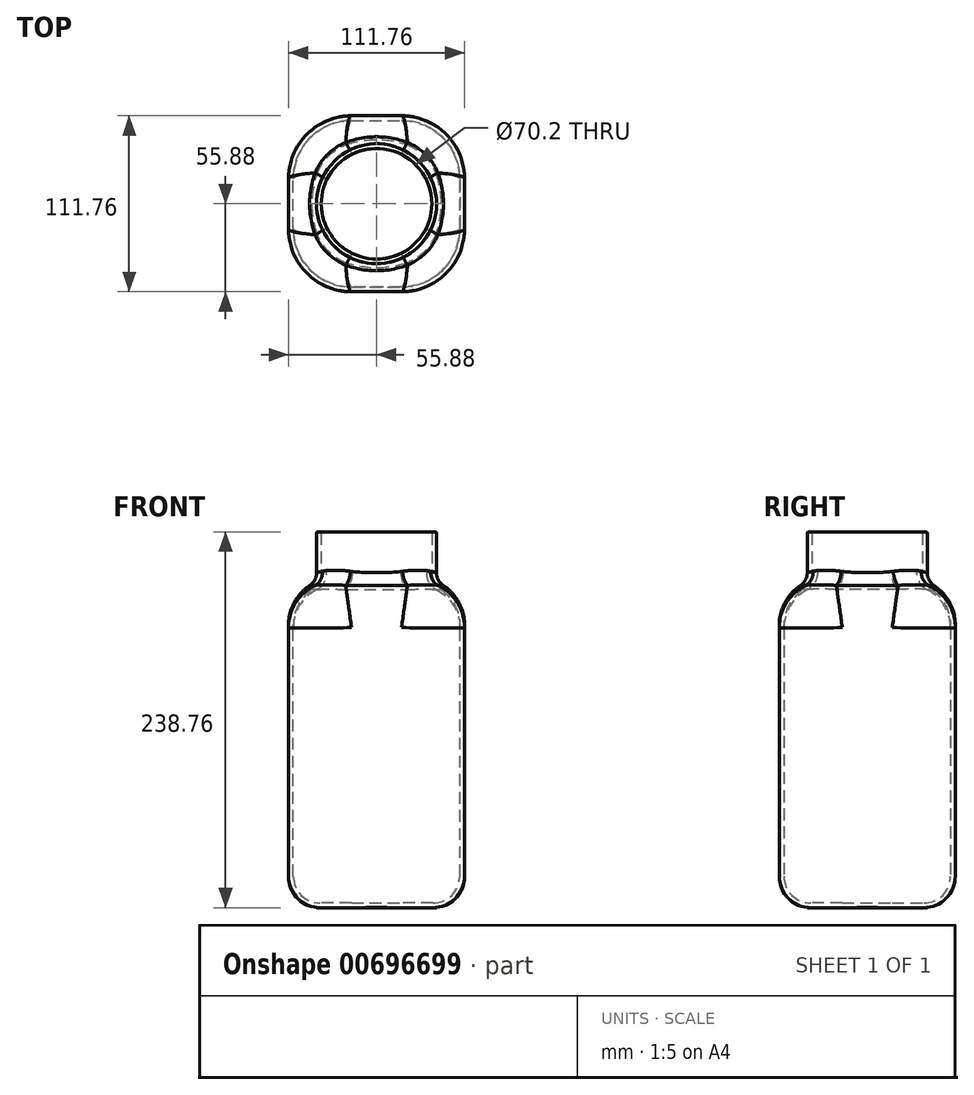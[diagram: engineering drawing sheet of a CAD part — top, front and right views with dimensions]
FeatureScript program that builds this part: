
annotation { "Feature Type Name" : "Feature", "Feature Type Description" : "" }
export const myFeature = defineFeature(function(context is Context, id is Id, definition is map)
    precondition{}
    {
        {
            assignVariable(context, id + "F0", {"name" : "height", "anyValue" : 238.76 * mm});
        }
        {
            var Q0;
            Q0=qCreatedBy(makeId("Top.planeOp"),FACE);
            var sketch = newSketch(context, id + "F1", { "sketchPlane" : qUnion([Q0])});
            skLineSegment(sketch, "E0.bottom", {"start": v(55.88, -55.88) * mm, "end": v(-55.88, -55.88) * mm});
            skLineSegment(sketch, "E0.top", {"start": v(55.88, 55.88) * mm, "end": v(-55.88, 55.88) * mm});
            skLineSegment(sketch, "E0.left", {"start": v(55.88, -55.88) * mm, "end": v(55.88, 55.88) * mm});
            skLineSegment(sketch, "E0.right", {"start": v(-55.88, -55.88) * mm, "end": v(-55.88, 55.88) * mm});
            skPoint(sketch, "E0.middle", {"position": v(0, 0) * mm});
            skCircle(sketch, "E1", {"center": v(0, 0) * mm, "radius": 38.1 * mm});
            skSolve(sketch);
        }
        {
            var Q0;
            Q0=makeQuery(id+"F1.imprint","IMPRINT",FACE,{"disambiguationData":[TD([[makeQuery(id+"F1.imprint","IMPRINT",EDGE,{"derivedFrom":sQuery(id+"F1.wireOp",EDGE,"E0.bottom")}),-1.0]])]});
            extrude(context, id + "F2", {"entities" : qUnion([Q0]), "depth" : getVariable(context, 'height') - 31.75 * mm, "offsetDistance" : 25 * mm});
        }
        {
            var Q0;
            Q0=makeQuery(id+"F2.opExtrude","SWEPT_EDGE",EDGE,{"disambiguationData":[OSD([sQuery(id+"F1.wireOp",EDGE,"E0.bottom"),sQuery(id+"F1.wireOp",EDGE,"E0.left")])]});
            var Q1;
            Q1=makeQuery(id+"F2.opExtrude","SWEPT_EDGE",EDGE,{"disambiguationData":[OSD([sQuery(id+"F1.wireOp",EDGE,"E0.top"),sQuery(id+"F1.wireOp",EDGE,"E0.left")])]});
            var Q2;
            Q2=makeQuery(id+"F2.opExtrude","SWEPT_EDGE",EDGE,{"disambiguationData":[OSD([sQuery(id+"F1.wireOp",EDGE,"E0.top"),sQuery(id+"F1.wireOp",EDGE,"E0.right")])]});
            var Q3;
            Q3=makeQuery(id+"F2.opExtrude","SWEPT_EDGE",EDGE,{"disambiguationData":[OSD([sQuery(id+"F1.wireOp",EDGE,"E0.bottom"),sQuery(id+"F1.wireOp",EDGE,"E0.right")])]});
            fillet(context, id + "F3", {"entities" : qUnion([Q0, Q1, Q2, Q3]), "radius" : 40 * mm, "tangentPropagation" : true, "allowEdgeOverflow" : false});
        }
        {
            var Q0;
            Q0=makeQuery(id+"F2.opExtrude","CAP_EDGE",EDGE,{"disambiguationData":[OSD([sQuery(id+"F1.wireOp",EDGE,"E0.top")])],"isStart":true});
            var Q1;
            {var subQ0=sQuery(id+"F1.wireOp",EDGE,"E0.right");var subQ1=sQuery(id+"F1.wireOp",EDGE,"E0.top");Q1=makeQuery(id+"F3.opFillet","BLEND_EDGE",EDGE,{"blendedFrom":[makeQuery(id+"F2.opExtrude","SWEPT_EDGE",EDGE,{"disambiguationData":[OSD([subQ1,subQ0])]}),makeQuery(id+"F2.opExtrude","CAP_FACE",FACE,{"disambiguationData":[OSD([sQuery(id+"F1.wireOp",EDGE,"E0.bottom"),subQ1,sQuery(id+"F1.wireOp",EDGE,"E0.left"),subQ0])],"isStart":true})],"blendedInto":[makeQuery(id+"F2.opExtrude","CAP_FACE",FACE,{"disambiguationData":[OSD([sQuery(id+"F1.wireOp",EDGE,"E0.bottom"),subQ1,sQuery(id+"F1.wireOp",EDGE,"E0.left"),subQ0])],"isStart":true})]});}
            var Q2;
            Q2=makeQuery(id+"F2.opExtrude","CAP_EDGE",EDGE,{"disambiguationData":[OSD([sQuery(id+"F1.wireOp",EDGE,"E0.right")])],"isStart":true});
            var Q3;
            {var subQ0=sQuery(id+"F1.wireOp",EDGE,"E0.right");var subQ1=sQuery(id+"F1.wireOp",EDGE,"E0.bottom");Q3=makeQuery(id+"F3.opFillet","BLEND_EDGE",EDGE,{"blendedFrom":[makeQuery(id+"F2.opExtrude","SWEPT_EDGE",EDGE,{"disambiguationData":[OSD([subQ1,subQ0])]}),makeQuery(id+"F2.opExtrude","CAP_FACE",FACE,{"disambiguationData":[OSD([subQ1,sQuery(id+"F1.wireOp",EDGE,"E0.top"),sQuery(id+"F1.wireOp",EDGE,"E0.left"),subQ0])],"isStart":true})],"blendedInto":[makeQuery(id+"F2.opExtrude","CAP_FACE",FACE,{"disambiguationData":[OSD([subQ1,sQuery(id+"F1.wireOp",EDGE,"E0.top"),sQuery(id+"F1.wireOp",EDGE,"E0.left"),subQ0])],"isStart":true})]});}
            var Q4;
            {var subQ0=sQuery(id+"F1.wireOp",EDGE,"E0.left");var subQ1=sQuery(id+"F1.wireOp",EDGE,"E0.top");Q4=makeQuery(id+"F3.opFillet","BLEND_EDGE",EDGE,{"blendedFrom":[makeQuery(id+"F2.opExtrude","SWEPT_EDGE",EDGE,{"disambiguationData":[OSD([subQ1,subQ0])]}),makeQuery(id+"F2.opExtrude","CAP_FACE",FACE,{"disambiguationData":[OSD([sQuery(id+"F1.wireOp",EDGE,"E0.bottom"),subQ1,subQ0,sQuery(id+"F1.wireOp",EDGE,"E0.right")])],"isStart":true})],"blendedInto":[makeQuery(id+"F2.opExtrude","CAP_FACE",FACE,{"disambiguationData":[OSD([sQuery(id+"F1.wireOp",EDGE,"E0.bottom"),subQ1,subQ0,sQuery(id+"F1.wireOp",EDGE,"E0.right")])],"isStart":true})]});}
            var Q5;
            Q5=makeQuery(id+"F2.opExtrude","CAP_EDGE",EDGE,{"disambiguationData":[OSD([sQuery(id+"F1.wireOp",EDGE,"E0.left")])],"isStart":true});
            var Q6;
            {var subQ0=sQuery(id+"F1.wireOp",EDGE,"E0.left");var subQ1=sQuery(id+"F1.wireOp",EDGE,"E0.bottom");Q6=makeQuery(id+"F3.opFillet","BLEND_EDGE",EDGE,{"blendedFrom":[makeQuery(id+"F2.opExtrude","SWEPT_EDGE",EDGE,{"disambiguationData":[OSD([subQ1,subQ0])]}),makeQuery(id+"F2.opExtrude","CAP_FACE",FACE,{"disambiguationData":[OSD([subQ1,sQuery(id+"F1.wireOp",EDGE,"E0.top"),subQ0,sQuery(id+"F1.wireOp",EDGE,"E0.right")])],"isStart":true})],"blendedInto":[makeQuery(id+"F2.opExtrude","CAP_FACE",FACE,{"disambiguationData":[OSD([subQ1,sQuery(id+"F1.wireOp",EDGE,"E0.top"),subQ0,sQuery(id+"F1.wireOp",EDGE,"E0.right")])],"isStart":true})]});}
            var Q7;
            Q7=makeQuery(id+"F2.opExtrude","CAP_EDGE",EDGE,{"disambiguationData":[OSD([sQuery(id+"F1.wireOp",EDGE,"E0.bottom")])],"isStart":true});
            fillet(context, id + "F4", {"entities" : qUnion([Q0, Q1, Q2, Q3, Q4, Q5, Q6, Q7]), "radius" : 20 * mm, "tangentPropagation" : true, "allowEdgeOverflow" : false});
        }
        {
            var Q0;
            Q0=makeQuery(id+"F1.imprint","IMPRINT",FACE,{"disambiguationData":[TD([[makeQuery(id+"F1.imprint","IMPRINT",EDGE,{"derivedFrom":sQuery(id+"F1.wireOp",EDGE,"E1")}),1.0]])]});
            extrude(context, id + "F5", {"entities" : qUnion([Q0]), "operationType" : NewBodyOperationType.ADD, "depth" : getVariable(context, 'height'), "offsetDistance" : 25 * mm});
        }
        {
            var Q0;
            {var subQ0=sQuery(id+"F1.wireOp",EDGE,"E0.left");var subQ1=sQuery(id+"F1.wireOp",EDGE,"E0.bottom");Q0=makeQuery(id+"F3.opFillet","BLEND_EDGE",EDGE,{"blendedFrom":[makeQuery(id+"F2.opExtrude","SWEPT_EDGE",EDGE,{"disambiguationData":[OSD([subQ1,subQ0])]}),makeQuery(id+"F2.opExtrude","CAP_FACE",FACE,{"disambiguationData":[OSD([subQ1,sQuery(id+"F1.wireOp",EDGE,"E0.top"),subQ0,sQuery(id+"F1.wireOp",EDGE,"E0.right"),sQuery(id+"F1.wireOp",EDGE,"E1")])],"isStart":false})],"blendedInto":[makeQuery(id+"F2.opExtrude","CAP_FACE",FACE,{"disambiguationData":[OSD([subQ1,sQuery(id+"F1.wireOp",EDGE,"E0.top"),subQ0,sQuery(id+"F1.wireOp",EDGE,"E0.right"),sQuery(id+"F1.wireOp",EDGE,"E1")])],"isStart":false})]});}
            var Q1;
            Q1=makeQuery(id+"F2.opExtrude","CAP_EDGE",EDGE,{"disambiguationData":[OSD([sQuery(id+"F1.wireOp",EDGE,"E0.bottom")])],"isStart":false});
            var Q2;
            {var subQ0=sQuery(id+"F1.wireOp",EDGE,"E0.right");var subQ1=sQuery(id+"F1.wireOp",EDGE,"E0.bottom");Q2=makeQuery(id+"F3.opFillet","BLEND_EDGE",EDGE,{"blendedFrom":[makeQuery(id+"F2.opExtrude","SWEPT_EDGE",EDGE,{"disambiguationData":[OSD([subQ1,subQ0])]}),makeQuery(id+"F2.opExtrude","CAP_FACE",FACE,{"disambiguationData":[OSD([subQ1,sQuery(id+"F1.wireOp",EDGE,"E0.top"),sQuery(id+"F1.wireOp",EDGE,"E0.left"),subQ0,sQuery(id+"F1.wireOp",EDGE,"E1")])],"isStart":false})],"blendedInto":[makeQuery(id+"F2.opExtrude","CAP_FACE",FACE,{"disambiguationData":[OSD([subQ1,sQuery(id+"F1.wireOp",EDGE,"E0.top"),sQuery(id+"F1.wireOp",EDGE,"E0.left"),subQ0,sQuery(id+"F1.wireOp",EDGE,"E1")])],"isStart":false})]});}
            var Q3;
            Q3=makeQuery(id+"F2.opExtrude","CAP_EDGE",EDGE,{"disambiguationData":[OSD([sQuery(id+"F1.wireOp",EDGE,"E0.left")])],"isStart":false});
            var Q4;
            {var subQ0=sQuery(id+"F1.wireOp",EDGE,"E0.left");var subQ1=sQuery(id+"F1.wireOp",EDGE,"E0.top");Q4=makeQuery(id+"F3.opFillet","BLEND_EDGE",EDGE,{"blendedFrom":[makeQuery(id+"F2.opExtrude","SWEPT_EDGE",EDGE,{"disambiguationData":[OSD([subQ1,subQ0])]}),makeQuery(id+"F2.opExtrude","CAP_FACE",FACE,{"disambiguationData":[OSD([sQuery(id+"F1.wireOp",EDGE,"E0.bottom"),subQ1,subQ0,sQuery(id+"F1.wireOp",EDGE,"E0.right"),sQuery(id+"F1.wireOp",EDGE,"E1")])],"isStart":false})],"blendedInto":[makeQuery(id+"F2.opExtrude","CAP_FACE",FACE,{"disambiguationData":[OSD([sQuery(id+"F1.wireOp",EDGE,"E0.bottom"),subQ1,subQ0,sQuery(id+"F1.wireOp",EDGE,"E0.right"),sQuery(id+"F1.wireOp",EDGE,"E1")])],"isStart":false})]});}
            var Q5;
            Q5=makeQuery(id+"F2.opExtrude","CAP_EDGE",EDGE,{"disambiguationData":[OSD([sQuery(id+"F1.wireOp",EDGE,"E0.right")])],"isStart":false});
            var Q6;
            Q6=makeQuery(id+"F2.opExtrude","CAP_EDGE",EDGE,{"disambiguationData":[OSD([sQuery(id+"F1.wireOp",EDGE,"E0.top")])],"isStart":false});
            var Q7;
            {var subQ0=sQuery(id+"F1.wireOp",EDGE,"E0.right");var subQ1=sQuery(id+"F1.wireOp",EDGE,"E0.top");Q7=makeQuery(id+"F3.opFillet","BLEND_EDGE",EDGE,{"blendedFrom":[makeQuery(id+"F2.opExtrude","SWEPT_EDGE",EDGE,{"disambiguationData":[OSD([subQ1,subQ0])]}),makeQuery(id+"F2.opExtrude","CAP_FACE",FACE,{"disambiguationData":[OSD([sQuery(id+"F1.wireOp",EDGE,"E0.bottom"),subQ1,sQuery(id+"F1.wireOp",EDGE,"E0.left"),subQ0,sQuery(id+"F1.wireOp",EDGE,"E1")])],"isStart":false})],"blendedInto":[makeQuery(id+"F2.opExtrude","CAP_FACE",FACE,{"disambiguationData":[OSD([sQuery(id+"F1.wireOp",EDGE,"E0.bottom"),subQ1,sQuery(id+"F1.wireOp",EDGE,"E0.left"),subQ0,sQuery(id+"F1.wireOp",EDGE,"E1")])],"isStart":false})]});}
            fillet(context, id + "F6", {"entities" : qUnion([Q0, Q1, Q2, Q3, Q4, Q5, Q6, Q7]), "radius" : 30 * mm, "tangentPropagation" : true, "allowEdgeOverflow" : false});
        }
        {
            var Q0;
            {var subQ0=sQuery(id+"F1.wireOp",EDGE,"E1");var subQ1=sQuery(id+"F1.wireOp",EDGE,"E0.left");var subQ2=sQuery(id+"F1.wireOp",EDGE,"E0.top");var subQ3=makeQuery(id+"F2.opExtrude","CAP_FACE",FACE,{"disambiguationData":[OSD([sQuery(id+"F1.wireOp",EDGE,"E0.bottom"),subQ2,subQ1,sQuery(id+"F1.wireOp",EDGE,"E0.right"),subQ0])],"isStart":false});Q0=makeQuery(id+"F6.opFillet","BLEND_EDGE",EDGE,{"blendedFrom":[makeQuery(id+"F3.opFillet","BLEND_EDGE",EDGE,{"blendedFrom":[makeQuery(id+"F2.opExtrude","SWEPT_EDGE",EDGE,{"disambiguationData":[OSD([subQ2,subQ1])]}),subQ3],"blendedInto":[subQ3]}),makeQuery(id+"F5.boolean.opBoolean","SPLIT",FACE,{"disambiguationData":[TD([makeQuery(id+"F5.opExtrude","CAP_FACE",FACE,{"disambiguationData":[OSD([subQ0])],"isStart":false})])],"derivedFrom":makeQuery(id+"F5.opExtrude","SWEPT_FACE",FACE,{"disambiguationData":[OSD([subQ0])]})})],"blendedInto":[makeQuery(id+"F5.boolean.opBoolean","SPLIT",FACE,{"disambiguationData":[TD([makeQuery(id+"F5.opExtrude","CAP_FACE",FACE,{"disambiguationData":[OSD([subQ0])],"isStart":false})])],"derivedFrom":makeQuery(id+"F5.opExtrude","SWEPT_FACE",FACE,{"disambiguationData":[OSD([subQ0])]})})]});}
            var Q1;
            {var subQ0=sQuery(id+"F1.wireOp",EDGE,"E1");var subQ1=sQuery(id+"F1.wireOp",EDGE,"E0.top");Q1=makeQuery(id+"F6.opFillet","BLEND_EDGE",EDGE,{"blendedFrom":[makeQuery(id+"F2.opExtrude","CAP_EDGE",EDGE,{"disambiguationData":[OSD([subQ1])],"isStart":false}),makeQuery(id+"F5.boolean.opBoolean","SPLIT",FACE,{"disambiguationData":[TD([makeQuery(id+"F5.opExtrude","CAP_FACE",FACE,{"disambiguationData":[OSD([subQ0])],"isStart":false})])],"derivedFrom":makeQuery(id+"F5.opExtrude","SWEPT_FACE",FACE,{"disambiguationData":[OSD([subQ0])]})})],"blendedInto":[makeQuery(id+"F5.boolean.opBoolean","SPLIT",FACE,{"disambiguationData":[TD([makeQuery(id+"F5.opExtrude","CAP_FACE",FACE,{"disambiguationData":[OSD([subQ0])],"isStart":false})])],"derivedFrom":makeQuery(id+"F5.opExtrude","SWEPT_FACE",FACE,{"disambiguationData":[OSD([subQ0])]})})]});}
            var Q2;
            {var subQ0=sQuery(id+"F1.wireOp",EDGE,"E1");var subQ1=sQuery(id+"F1.wireOp",EDGE,"E0.left");Q2=makeQuery(id+"F6.opFillet","BLEND_EDGE",EDGE,{"blendedFrom":[makeQuery(id+"F2.opExtrude","CAP_EDGE",EDGE,{"disambiguationData":[OSD([subQ1])],"isStart":false}),makeQuery(id+"F5.boolean.opBoolean","SPLIT",FACE,{"disambiguationData":[TD([makeQuery(id+"F5.opExtrude","CAP_FACE",FACE,{"disambiguationData":[OSD([subQ0])],"isStart":false})])],"derivedFrom":makeQuery(id+"F5.opExtrude","SWEPT_FACE",FACE,{"disambiguationData":[OSD([subQ0])]})})],"blendedInto":[makeQuery(id+"F5.boolean.opBoolean","SPLIT",FACE,{"disambiguationData":[TD([makeQuery(id+"F5.opExtrude","CAP_FACE",FACE,{"disambiguationData":[OSD([subQ0])],"isStart":false})])],"derivedFrom":makeQuery(id+"F5.opExtrude","SWEPT_FACE",FACE,{"disambiguationData":[OSD([subQ0])]})})]});}
            var Q3;
            {var subQ0=sQuery(id+"F1.wireOp",EDGE,"E1");var subQ1=sQuery(id+"F1.wireOp",EDGE,"E0.right");var subQ2=sQuery(id+"F1.wireOp",EDGE,"E0.top");var subQ3=makeQuery(id+"F2.opExtrude","CAP_FACE",FACE,{"disambiguationData":[OSD([sQuery(id+"F1.wireOp",EDGE,"E0.bottom"),subQ2,sQuery(id+"F1.wireOp",EDGE,"E0.left"),subQ1,subQ0])],"isStart":false});Q3=makeQuery(id+"F6.opFillet","BLEND_EDGE",EDGE,{"blendedFrom":[makeQuery(id+"F3.opFillet","BLEND_EDGE",EDGE,{"blendedFrom":[makeQuery(id+"F2.opExtrude","SWEPT_EDGE",EDGE,{"disambiguationData":[OSD([subQ2,subQ1])]}),subQ3],"blendedInto":[subQ3]}),makeQuery(id+"F5.boolean.opBoolean","SPLIT",FACE,{"disambiguationData":[TD([makeQuery(id+"F5.opExtrude","CAP_FACE",FACE,{"disambiguationData":[OSD([subQ0])],"isStart":false})])],"derivedFrom":makeQuery(id+"F5.opExtrude","SWEPT_FACE",FACE,{"disambiguationData":[OSD([subQ0])]})})],"blendedInto":[makeQuery(id+"F5.boolean.opBoolean","SPLIT",FACE,{"disambiguationData":[TD([makeQuery(id+"F5.opExtrude","CAP_FACE",FACE,{"disambiguationData":[OSD([subQ0])],"isStart":false})])],"derivedFrom":makeQuery(id+"F5.opExtrude","SWEPT_FACE",FACE,{"disambiguationData":[OSD([subQ0])]})})]});}
            var Q4;
            {var subQ0=sQuery(id+"F1.wireOp",EDGE,"E1");var subQ1=sQuery(id+"F1.wireOp",EDGE,"E0.right");Q4=makeQuery(id+"F6.opFillet","BLEND_EDGE",EDGE,{"blendedFrom":[makeQuery(id+"F2.opExtrude","CAP_EDGE",EDGE,{"disambiguationData":[OSD([subQ1])],"isStart":false}),makeQuery(id+"F5.boolean.opBoolean","SPLIT",FACE,{"disambiguationData":[TD([makeQuery(id+"F5.opExtrude","CAP_FACE",FACE,{"disambiguationData":[OSD([subQ0])],"isStart":false})])],"derivedFrom":makeQuery(id+"F5.opExtrude","SWEPT_FACE",FACE,{"disambiguationData":[OSD([subQ0])]})})],"blendedInto":[makeQuery(id+"F5.boolean.opBoolean","SPLIT",FACE,{"disambiguationData":[TD([makeQuery(id+"F5.opExtrude","CAP_FACE",FACE,{"disambiguationData":[OSD([subQ0])],"isStart":false})])],"derivedFrom":makeQuery(id+"F5.opExtrude","SWEPT_FACE",FACE,{"disambiguationData":[OSD([subQ0])]})})]});}
            var Q5;
            {var subQ0=sQuery(id+"F1.wireOp",EDGE,"E1");var subQ1=sQuery(id+"F1.wireOp",EDGE,"E0.right");var subQ2=sQuery(id+"F1.wireOp",EDGE,"E0.bottom");var subQ3=makeQuery(id+"F2.opExtrude","CAP_FACE",FACE,{"disambiguationData":[OSD([subQ2,sQuery(id+"F1.wireOp",EDGE,"E0.top"),sQuery(id+"F1.wireOp",EDGE,"E0.left"),subQ1,subQ0])],"isStart":false});Q5=makeQuery(id+"F6.opFillet","BLEND_EDGE",EDGE,{"blendedFrom":[makeQuery(id+"F3.opFillet","BLEND_EDGE",EDGE,{"blendedFrom":[makeQuery(id+"F2.opExtrude","SWEPT_EDGE",EDGE,{"disambiguationData":[OSD([subQ2,subQ1])]}),subQ3],"blendedInto":[subQ3]}),makeQuery(id+"F5.boolean.opBoolean","SPLIT",FACE,{"disambiguationData":[TD([makeQuery(id+"F5.opExtrude","CAP_FACE",FACE,{"disambiguationData":[OSD([subQ0])],"isStart":false})])],"derivedFrom":makeQuery(id+"F5.opExtrude","SWEPT_FACE",FACE,{"disambiguationData":[OSD([subQ0])]})})],"blendedInto":[makeQuery(id+"F5.boolean.opBoolean","SPLIT",FACE,{"disambiguationData":[TD([makeQuery(id+"F5.opExtrude","CAP_FACE",FACE,{"disambiguationData":[OSD([subQ0])],"isStart":false})])],"derivedFrom":makeQuery(id+"F5.opExtrude","SWEPT_FACE",FACE,{"disambiguationData":[OSD([subQ0])]})})]});}
            var Q6;
            {var subQ0=sQuery(id+"F1.wireOp",EDGE,"E1");var subQ1=sQuery(id+"F1.wireOp",EDGE,"E0.bottom");Q6=makeQuery(id+"F6.opFillet","BLEND_EDGE",EDGE,{"blendedFrom":[makeQuery(id+"F2.opExtrude","CAP_EDGE",EDGE,{"disambiguationData":[OSD([subQ1])],"isStart":false}),makeQuery(id+"F5.boolean.opBoolean","SPLIT",FACE,{"disambiguationData":[TD([makeQuery(id+"F5.opExtrude","CAP_FACE",FACE,{"disambiguationData":[OSD([subQ0])],"isStart":false})])],"derivedFrom":makeQuery(id+"F5.opExtrude","SWEPT_FACE",FACE,{"disambiguationData":[OSD([subQ0])]})})],"blendedInto":[makeQuery(id+"F5.boolean.opBoolean","SPLIT",FACE,{"disambiguationData":[TD([makeQuery(id+"F5.opExtrude","CAP_FACE",FACE,{"disambiguationData":[OSD([subQ0])],"isStart":false})])],"derivedFrom":makeQuery(id+"F5.opExtrude","SWEPT_FACE",FACE,{"disambiguationData":[OSD([subQ0])]})})]});}
            var Q7;
            {var subQ0=sQuery(id+"F1.wireOp",EDGE,"E1");var subQ1=sQuery(id+"F1.wireOp",EDGE,"E0.left");var subQ2=sQuery(id+"F1.wireOp",EDGE,"E0.bottom");var subQ3=makeQuery(id+"F2.opExtrude","CAP_FACE",FACE,{"disambiguationData":[OSD([subQ2,sQuery(id+"F1.wireOp",EDGE,"E0.top"),subQ1,sQuery(id+"F1.wireOp",EDGE,"E0.right"),subQ0])],"isStart":false});Q7=makeQuery(id+"F6.opFillet","BLEND_EDGE",EDGE,{"blendedFrom":[makeQuery(id+"F3.opFillet","BLEND_EDGE",EDGE,{"blendedFrom":[makeQuery(id+"F2.opExtrude","SWEPT_EDGE",EDGE,{"disambiguationData":[OSD([subQ2,subQ1])]}),subQ3],"blendedInto":[subQ3]}),makeQuery(id+"F5.boolean.opBoolean","SPLIT",FACE,{"disambiguationData":[TD([makeQuery(id+"F5.opExtrude","CAP_FACE",FACE,{"disambiguationData":[OSD([subQ0])],"isStart":false})])],"derivedFrom":makeQuery(id+"F5.opExtrude","SWEPT_FACE",FACE,{"disambiguationData":[OSD([subQ0])]})})],"blendedInto":[makeQuery(id+"F5.boolean.opBoolean","SPLIT",FACE,{"disambiguationData":[TD([makeQuery(id+"F5.opExtrude","CAP_FACE",FACE,{"disambiguationData":[OSD([subQ0])],"isStart":false})])],"derivedFrom":makeQuery(id+"F5.opExtrude","SWEPT_FACE",FACE,{"disambiguationData":[OSD([subQ0])]})})]});}
            fillet(context, id + "F7", {"entities" : qUnion([Q0, Q1, Q2, Q3, Q4, Q5, Q6, Q7]), "radius" : 10 * mm, "tangentPropagation" : true, "allowEdgeOverflow" : false});
        }
        {
            var Q0;
            Q0=makeQuery(id+"F5.opExtrude","CAP_FACE",FACE,{"disambiguationData":[OSD([sQuery(id+"F1.wireOp",EDGE,"E1")])],"isStart":false});
            shell(context, id + "F8", {"entities" : qUnion([Q0]), "thickness" : 3 * mm});
        }
        {
            var Q0;
            Q0=makeQuery(id+"F5.opExtrude","CAP_EDGE",EDGE,{"disambiguationData":[OSD([sQuery(id+"F1.wireOp",EDGE,"E1")])],"isStart":false});
            var Q1;
            {var subQ0=sQuery(id+"F1.wireOp",EDGE,"E1");Q1=makeQuery(id+"F8.opShell","OFFSET_EDGE",EDGE,{"disambiguationData":[OSD([subQ0]),TDD([makeQuery(id+"F5.opExtrude","CAP_EDGE",EDGE,{"disambiguationData":[OSD([subQ0])],"isStart":false})])]});}
            fillet(context, id + "F9", {"entities" : qUnion([Q0, Q1]), "radius" : 1 * mm, "tangentPropagation" : true, "allowEdgeOverflow" : false});
        }
    });
